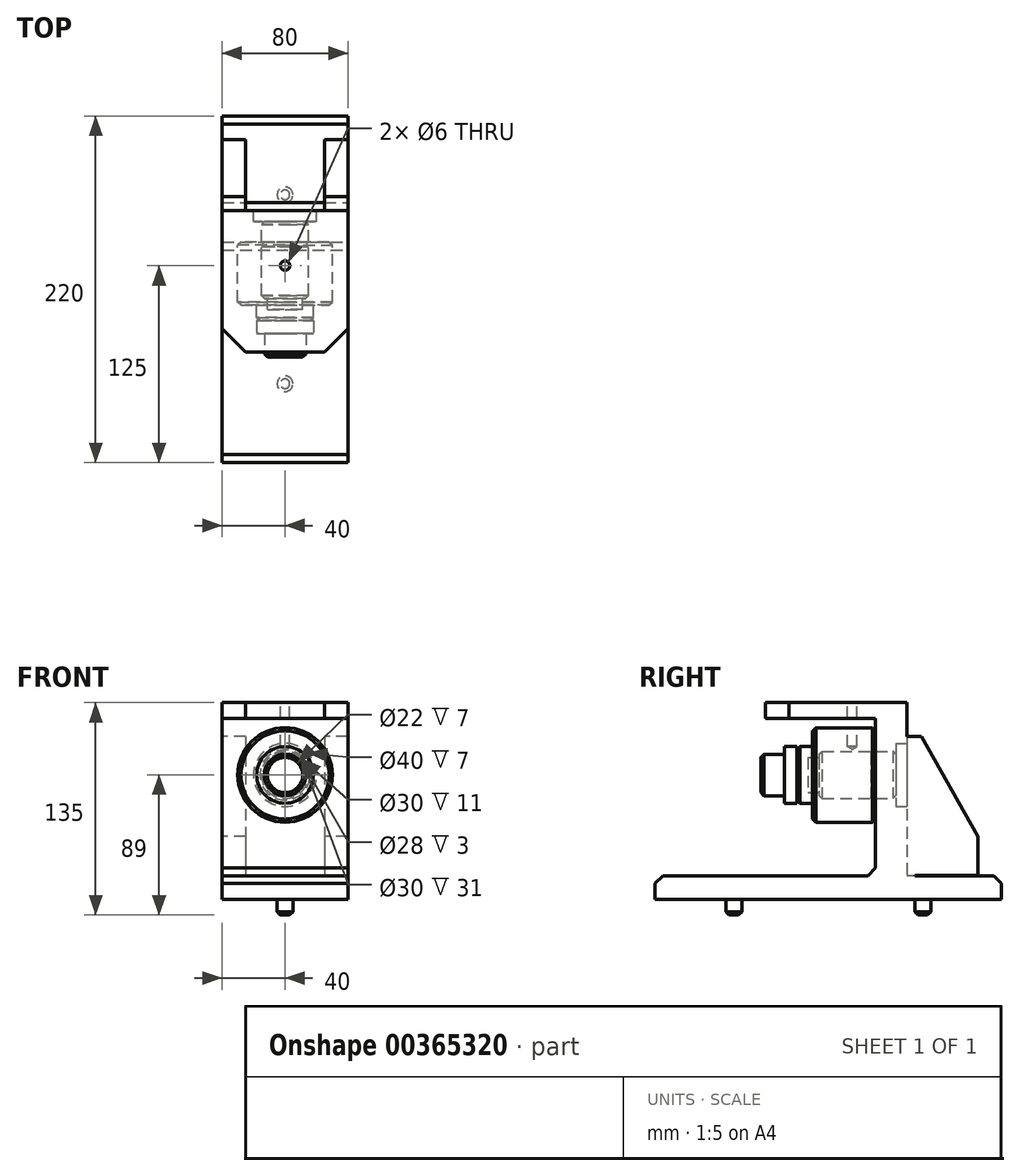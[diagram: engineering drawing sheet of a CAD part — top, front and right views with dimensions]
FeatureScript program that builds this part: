
annotation { "Feature Type Name" : "Feature", "Feature Type Description" : "" }
export const myFeature = defineFeature(function(context is Context, id is Id, definition is map)
    precondition{}
    {
        {
            var Q0;
            Q0=qCreatedBy(makeId("Right.planeOp"),FACE);
            var sketch = newSketch(context, id + "F0", { "sketchPlane" : qUnion([Q0])});
            skLineSegment(sketch, "E0", {"start": v(-10, 11) * mm, "end": v(-10, 18) * mm});
            skLineSegment(sketch, "E1", {"start": v(-10, 18) * mm, "end": v(0, 18) * mm});
            skLineSegment(sketch, "E2", {"start": v(0, 18) * mm, "end": v(0, 30) * mm});
            skLineSegment(sketch, "E3", {"start": v(0, 30) * mm, "end": v(40, 30) * mm});
            skLineSegment(sketch, "E4", {"start": v(40, 30) * mm, "end": v(40, 11) * mm});
            skLineSegment(sketch, "E5", {"start": v(40, 0) * mm, "end": v(-10, 0) * mm});
            skLineSegment(sketch, "E6", {"start": v(-10, 11) * mm, "end": v(40, 11) * mm});
            skSolve(sketch);
        }
        {
            var Q0;
            Q0=makeQuery(id+"F0.imprint","IMPRINT",FACE,{"disambiguationData":[TD([[makeQuery(id+"F0.imprint","IMPRINT",EDGE,{"derivedFrom":sQuery(id+"F0.wireOp",EDGE,"E0")}),-1.0]])]});
            var Q1;
            Q1=sQuery(id+"F0.wireOp",EDGE,"E5");
            revolve(context, id + "F1", {"entities" : qUnion([Q0]), "axis" : qUnion([Q1]), "revolveType" : RevolveType.FULL});
        }
        {
            var Q0;
            Q0=makeQuery(id+"F1.opRevolve","SWEPT_EDGE",EDGE,{"disambiguationData":[OSD([sQuery(id+"F0.wireOp",EDGE,"E0"),sQuery(id+"F0.wireOp",EDGE,"E1")])]});
            var Q1;
            Q1=makeQuery(id+"F1.opRevolve","SWEPT_EDGE",EDGE,{"disambiguationData":[OSD([sQuery(id+"F0.wireOp",EDGE,"E2"),sQuery(id+"F0.wireOp",EDGE,"E3")])]});
            var Q2;
            Q2=makeQuery(id+"F1.opRevolve","SWEPT_EDGE",EDGE,{"disambiguationData":[OSD([sQuery(id+"F0.wireOp",EDGE,"E3"),sQuery(id+"F0.wireOp",EDGE,"E4")])]});
            chamfer(context, id + "F2", {"entities" : qUnion([Q0, Q1, Q2]), "width" : 2 * mm, "tangentPropagation" : true});
        }
        {
            var Q0;
            Q0=qCreatedBy(makeId("Right.planeOp"),FACE);
            var sketch = newSketch(context, id + "F3", { "sketchPlane" : qUnion([Q0])});
            skLineSegment(sketch, "E7", {"start": v(25, 16.27) * mm, "end": v(25, 30) * mm});
            skLineSegment(sketch, "E8", {"start": v(22, 18) * mm, "end": v(22, 30) * mm});
            skLineSegment(sketch, "E9", {"start": v(22, 18) * mm, "end": v(25, 16.27) * mm});
            skPoint(sketch, "E10.orphan", {"position": v(22, 0) * mm});
            skPoint(sketch, "E11.orphan", {"position": v(25, 0) * mm});
            skLineSegment(sketch, "E12", {"start": v(22, 30) * mm, "end": v(25, 30) * mm});
            skSolve(sketch);
        }
        {
            var Q0;
            Q0 = qSketchRegion(id + "F3", true);
            var Q1;
            Q1=sQuery(id+"F3.wireOp",EDGE,"E7");
            revolve(context, id + "F4", {"operationType" : NewBodyOperationType.REMOVE, "entities" : qUnion([Q0]), "axis" : qUnion([Q1]), "revolveType" : RevolveType.FULL, "oppositeDirection" : true});
        }
        {
            var Q0;
            Q0=qCreatedBy(makeId("Top.planeOp"),FACE);
            cPlane(context, id + "F5", {"entities" : qUnion([Q0]), "cplaneType" : CPlaneType.OFFSET, "offset" : 46 * mm, "width" : 150 * mm, "height" : 150 * mm});
        }
        {
            var Q0;
            Q0=qCreatedBy(makeId("Right.planeOp"),FACE);
            var sketch = newSketch(context, id + "F6", { "sketchPlane" : qUnion([Q0])});
            skLineSegment(sketch, "E13", {"start": v(22, 36) * mm, "end": v(22, 46) * mm});
            skLineSegment(sketch, "E14", {"start": v(20, 36) * mm, "end": v(20, 46) * mm});
            skLineSegment(sketch, "E15", {"start": v(20, 46) * mm, "end": v(22, 46) * mm});
            skLineSegment(sketch, "E16", {"start": v(20, 36) * mm, "end": v(22, 36) * mm});
            skPoint(sketch, "E17.orphan", {"position": v(20, 0) * mm});
            skPoint(sketch, "E18.orphan", {"position": v(22, 0) * mm});
            skLineSegment(sketch, "E19", {"start": v(25, 45.98) * mm, "end": v(25, 35.98) * mm});
            skSolve(sketch);
        }
        {
            var Q0;
            Q0 = qSketchRegion(id + "F6", true);
            var Q1;
            Q1=sQuery(id+"F6.wireOp",EDGE,"E19");
            revolve(context, id + "F7", {"entities" : qUnion([Q0]), "axis" : qUnion([Q1]), "revolveType" : RevolveType.FULL});
        }
        {
            var Q0;
            Q0=qCreatedBy(id+"F5.planeOp",FACE);
            var sketch = newSketch(context, id + "F8", { "sketchPlane" : qUnion([Q0])});
            skLineSegment(sketch, "E20.bottom", {"start": v(-40, 60) * mm, "end": v(40, 60) * mm});
            skLineSegment(sketch, "E20.top", {"start": v(-40, -30) * mm, "end": v(40, -30) * mm});
            skLineSegment(sketch, "E20.left", {"start": v(-40, 60) * mm, "end": v(-40, -30) * mm});
            skLineSegment(sketch, "E20.right", {"start": v(40, 60) * mm, "end": v(40, -30) * mm});
            skCircle(sketch, "E21", {"center": v(0, 25) * mm, "radius": 5 * mm});
            skSolve(sketch);
        }
        {
            var Q0;
            Q0=makeQuery(id+"F8.imprint","IMPRINT",FACE,{"disambiguationData":[TD([[makeQuery(id+"F8.imprint","IMPRINT",EDGE,{"derivedFrom":sQuery(id+"F8.wireOp",EDGE,"E20.bottom")}),-1.0]])]});
            extrude(context, id + "F9", {"entities" : qUnion([Q0]), "operationType" : NewBodyOperationType.ADD, "oppositeDirection" : true, "depth" : 10 * mm});
        }
        {
            var Q0;
            Q0=makeQuery(id+"F9.opExtrude","SWEPT_EDGE",EDGE,{"disambiguationData":[OSD([sQuery(id+"F8.wireOp",EDGE,"E20.top"),sQuery(id+"F8.wireOp",EDGE,"E20.left")])]});
            var Q1;
            Q1=makeQuery(id+"F9.opExtrude","SWEPT_EDGE",EDGE,{"disambiguationData":[OSD([sQuery(id+"F8.wireOp",EDGE,"E20.top"),sQuery(id+"F8.wireOp",EDGE,"E20.right")])]});
            chamfer(context, id + "F10", {"entities" : qUnion([Q0, Q1]), "width" : 15 * mm, "tangentPropagation" : true});
        }
        {
            var Q0;
            Q0=qCreatedBy(makeId("Front.planeOp"),FACE);
            cPlane(context, id + "F11", {"entities" : qUnion([Q0]), "cplaneType" : CPlaneType.OFFSET, "offset" : 60 * mm, "oppositeDirection" : true, "width" : 150 * mm, "height" : 150 * mm});
        }
        {
            var Q0;
            Q0=qCreatedBy(id+"F11.planeOp",FACE);
            var sketch = newSketch(context, id + "F12", { "sketchPlane" : qUnion([Q0])});
            skLineSegment(sketch, "E22.bottom", {"start": v(-40, 36) * mm, "end": v(40, 36) * mm});
            skLineSegment(sketch, "E22.top", {"start": v(-40, -64) * mm, "end": v(40, -64) * mm});
            skLineSegment(sketch, "E22.left", {"start": v(-40, 36) * mm, "end": v(-40, -64) * mm});
            skLineSegment(sketch, "E22.right", {"start": v(40, 36) * mm, "end": v(40, -64) * mm});
            skSolve(sketch);
        }
        {
            var Q0;
            Q0=makeQuery(id+"F12.imprint","IMPRINT",FACE,{"disambiguationData":[TD([[makeQuery(id+"F12.imprint","IMPRINT",EDGE,{"derivedFrom":sQuery(id+"F12.wireOp",EDGE,"E22.bottom")}),-1.0]])]});
            extrude(context, id + "F13", {"entities" : qUnion([Q0]), "operationType" : NewBodyOperationType.ADD, "depth" : 20 * mm});
        }
        {
            var Q0;
            Q0=makeQuery(id+"F13.boolean.opBoolean","MERGE",FACE,{"derivedFrom":[makeQuery(id+"F9.opExtrude","SWEPT_FACE",FACE,{"disambiguationData":[OSD([sQuery(id+"F8.wireOp",EDGE,"E20.right")])]}),makeQuery(id+"F13.opExtrude","SWEPT_FACE",FACE,{"disambiguationData":[OSD([sQuery(id+"F12.wireOp",EDGE,"E22.right")])]})]});
            var sketch = newSketch(context, id + "F14", { "sketchPlane" : qUnion([Q0])});
            skLineSegment(sketch, "E23", {"start": v(40, -64) * mm, "end": v(35, -64) * mm});
            skLineSegment(sketch, "E24", {"start": v(35, -64) * mm, "end": v(40, -59) * mm});
            skLineSegment(sketch, "E25", {"start": v(60, -64) * mm, "end": v(65, -64) * mm});
            skLineSegment(sketch, "E26", {"start": v(65, -64) * mm, "end": v(60, -59) * mm});
            skSolve(sketch);
        }
        {
            var Q0;
            {var subQ0=sQuery(id+"F14.wireOp",EDGE,"E23");Q0=makeQuery(id+"F14.imprint","IMPRINT",FACE,{"disambiguationData":[TD([[makeQuery(id+"F14.imprint","IMPRINT",EDGE,{"derivedFrom":subQ0}),-1.0]])]});}
            var Q1;
            {var subQ0=sQuery(id+"F14.wireOp",EDGE,"E25");Q1=makeQuery(id+"F14.imprint","IMPRINT",FACE,{"disambiguationData":[TD([[makeQuery(id+"F14.imprint","IMPRINT",EDGE,{"derivedFrom":subQ0}),1.0]])]});}
            extrude(context, id + "F15", {"entities" : qUnion([Q0, Q1]), "operationType" : NewBodyOperationType.ADD, "oppositeDirection" : true, "depth" : 80 * mm});
        }
        {
            var Q0;
            Q0=qCreatedBy(makeId("Right.planeOp"),FACE);
            var sketch = newSketch(context, id + "F16", { "sketchPlane" : qUnion([Q0])});
            skLineSegment(sketch, "E27", {"start": v(60, 24.53) * mm, "end": v(69, 24.53) * mm});
            skLineSegment(sketch, "E28", {"start": v(69, 24.53) * mm, "end": v(105, -38.95) * mm});
            skLineSegment(sketch, "E29", {"start": v(105, -38.95) * mm, "end": v(105, -63.95) * mm});
            skLineSegment(sketch, "E30", {"start": v(60, -63.95) * mm, "end": v(105, -63.95) * mm});
            skLineSegment(sketch, "E31", {"start": v(60, 24.53) * mm, "end": v(60, -63.95) * mm});
            skSolve(sketch);
        }
        {
            var Q0;
            Q0=qCreatedBy(makeId("Front.planeOp"),FACE);
            var sketch = newSketch(context, id + "F17", { "sketchPlane" : qUnion([Q0])});
            skLineSegment(sketch, "E32.bottom", {"start": v(-40, -64) * mm, "end": v(40, -64) * mm});
            skLineSegment(sketch, "E32.top", {"start": v(-40, -79) * mm, "end": v(40, -79) * mm});
            skLineSegment(sketch, "E32.left", {"start": v(-40, -64) * mm, "end": v(-40, -79) * mm});
            skLineSegment(sketch, "E32.right", {"start": v(40, -64) * mm, "end": v(40, -79) * mm});
            skSolve(sketch);
        }
        {
            var Q0;
            Q0=makeQuery(id+"F17.imprint","IMPRINT",FACE,{"disambiguationData":[TD([[makeQuery(id+"F17.imprint","IMPRINT",EDGE,{"derivedFrom":sQuery(id+"F17.wireOp",EDGE,"E32.bottom")}),-1.0]])]});
            extrude(context, id + "F18", {"entities" : qUnion([Q0]), "operationType" : NewBodyOperationType.ADD, "oppositeDirection" : true, "depth" : 120 * mm, "hasSecondDirection" : true, "secondDirectionOppositeDirection" : false, "secondDirectionDepth" : 100 * mm});
        }
        {
            var Q0;
            Q0=makeQuery(id+"F18.opExtrude","CAP_EDGE",EDGE,{"disambiguationData":[OSD([sQuery(id+"F17.wireOp",EDGE,"E32.bottom")])],"isStart":false});
            var Q1;
            Q1=makeQuery(id+"F18.opExtrude","CAP_EDGE",EDGE,{"disambiguationData":[OSD([sQuery(id+"F17.wireOp",EDGE,"E32.bottom")])],"isStart":true});
            chamfer(context, id + "F19", {"entities" : qUnion([Q0, Q1]), "width" : 5 * mm, "tangentPropagation" : true});
        }
        {
            var Q0;
            Q0=makeQuery(id+"F18.opExtrude","SWEPT_FACE",FACE,{"disambiguationData":[OSD([sQuery(id+"F17.wireOp",EDGE,"E32.top")])]});
            var sketch = newSketch(context, id + "F20", { "sketchPlane" : qUnion([Q0])});
            skCircle(sketch, "E33", {"center": v(0, 50) * mm, "radius": 5 * mm});
            skCircle(sketch, "E34", {"center": v(0, -70) * mm, "radius": 5 * mm});
            skSolve(sketch);
        }
        {
            var Q0;
            Q0=makeQuery(id+"F20.imprint","IMPRINT",FACE,{"disambiguationData":[TD([[makeQuery(id+"F20.imprint","IMPRINT",EDGE,{"derivedFrom":sQuery(id+"F20.wireOp",EDGE,"E33")}),1.0]])]});
            var Q1;
            Q1=makeQuery(id+"F20.imprint","IMPRINT",FACE,{"disambiguationData":[TD([[makeQuery(id+"F20.imprint","IMPRINT",EDGE,{"derivedFrom":sQuery(id+"F20.wireOp",EDGE,"E34")}),1.0]])]});
            extrude(context, id + "F21", {"entities" : qUnion([Q0, Q1]), "operationType" : NewBodyOperationType.ADD, "depth" : 10 * mm});
        }
        {
            var Q0;
            Q0=makeQuery(id+"F21.opExtrude","CAP_EDGE",EDGE,{"disambiguationData":[OSD([sQuery(id+"F20.wireOp",EDGE,"E33")])],"isStart":false});
            var Q1;
            Q1=makeQuery(id+"F21.opExtrude","CAP_EDGE",EDGE,{"disambiguationData":[OSD([sQuery(id+"F20.wireOp",EDGE,"E34")])],"isStart":false});
            chamfer(context, id + "F22", {"entities" : qUnion([Q0, Q1]), "width" : 2 * mm, "tangentPropagation" : true});
        }
        {
            var Q0;
            Q0=makeQuery(id+"F16.imprint","IMPRINT",FACE,{"disambiguationData":[TD([[makeQuery(id+"F16.imprint","IMPRINT",EDGE,{"derivedFrom":sQuery(id+"F16.wireOp",EDGE,"E27")}),-1.0]])]});
            extrude(context, id + "F23", {"entities" : qUnion([Q0]), "operationType" : NewBodyOperationType.ADD, "depth" : 40 * mm, "hasSecondDirection" : true, "secondDirectionOppositeDirection" : true, "secondDirectionDepth" : 40 * mm});
        }
        {
            var Q0;
            Q0 = qSketchRegion(id + "F16", true);
            extrude(context, id + "F24", {"entities" : qUnion([Q0]), "operationType" : NewBodyOperationType.REMOVE, "depth" : 25 * mm, "hasSecondDirection" : true, "secondDirectionOppositeDirection" : true, "secondDirectionDepth" : 25 * mm});
        }
        {
            var Q0;
            Q0=qCreatedBy(makeId("Right.planeOp"),FACE);
            var sketch = newSketch(context, id + "F25", { "sketchPlane" : qUnion([Q0])});
            skLineSegment(sketch, "E35", {"start": v(60, 20) * mm, "end": v(53, 20) * mm});
            skLineSegment(sketch, "E36", {"start": v(53, 20) * mm, "end": v(53, 0) * mm});
            skLineSegment(sketch, "E37", {"start": v(60, 20) * mm, "end": v(60, 0) * mm});
            skLineSegment(sketch, "E38", {"start": v(53, 0) * mm, "end": v(60, 0) * mm});
            skPoint(sketch, "E38.endSnap0", {"position": v(60, 0) * mm});
            skPoint(sketch, "E39.orphan", {"position": v(62.1, 0) * mm});
            skPoint(sketch, "E40.end.orphan", {"position": v(60, -20) * mm});
            skPoint(sketch, "E40.start.orphan", {"position": v(53, -20) * mm});
            skSolve(sketch);
        }
        {
            var Q0;
            Q0 = qSketchRegion(id + "F25", true);
            var Q1;
            Q1=sQuery(id+"F25.wireOp",EDGE,"E38");
            revolve(context, id + "F26", {"operationType" : NewBodyOperationType.REMOVE, "entities" : qUnion([Q0]), "axis" : qUnion([Q1]), "revolveType" : RevolveType.FULL, "oppositeDirection" : true});
        }
        {
            var Q0;
            Q0=qCreatedBy(makeId("Right.planeOp"),FACE);
            var sketch = newSketch(context, id + "F27", { "sketchPlane" : qUnion([Q0])});
            skLineSegment(sketch, "E41", {"start": v(51, 15) * mm, "end": v(40, 15) * mm});
            skLineSegment(sketch, "E42", {"start": v(40, 15) * mm, "end": v(40, 14) * mm});
            skLineSegment(sketch, "E43", {"start": v(40, 14) * mm, "end": v(37, 14) * mm});
            skLineSegment(sketch, "E44", {"start": v(37, 14) * mm, "end": v(37, 15) * mm});
            skLineSegment(sketch, "E45", {"start": v(37, 15) * mm, "end": v(6, 15) * mm});
            skLineSegment(sketch, "E46", {"start": v(4, 13) * mm, "end": v(4, 0) * mm});
            skLineSegment(sketch, "E47", {"start": v(4, 0) * mm, "end": v(53, 0) * mm});
            skLineSegment(sketch, "E48", {"start": v(53, 13) * mm, "end": v(53, 0) * mm});
            skLineSegment(sketch, "E49", {"start": v(51, 15) * mm, "end": v(53, 13) * mm});
            skLineSegment(sketch, "E50", {"start": v(6, 15) * mm, "end": v(4, 13) * mm});
            skPoint(sketch, "E51.orphan", {"position": v(53, 15) * mm});
            skPoint(sketch, "E52.orphan", {"position": v(4, 15) * mm});
            skSolve(sketch);
        }
        {
            var Q0;
            Q0 = qSketchRegion(id + "F27", true);
            var Q1;
            Q1=sQuery(id+"F27.wireOp",EDGE,"E47");
            revolve(context, id + "F28", {"operationType" : NewBodyOperationType.REMOVE, "entities" : qUnion([Q0]), "axis" : qUnion([Q1]), "revolveType" : RevolveType.FULL, "oppositeDirection" : true});
        }
        {
            var Q0;
            Q0=qCreatedBy(makeId("Right.planeOp"),FACE);
            var sketch = newSketch(context, id + "F29", { "sketchPlane" : qUnion([Q0])});
            skLineSegment(sketch, "E53", {"start": v(-18, 13.18) * mm, "end": v(-18, 18) * mm});
            skLineSegment(sketch, "E54", {"start": v(-18, 18) * mm, "end": v(-10, 18) * mm});
            skLineSegment(sketch, "E55", {"start": v(-10, 18) * mm, "end": v(-10, 11) * mm});
            skLineSegment(sketch, "E56", {"start": v(-3, 11) * mm, "end": v(-10, 11) * mm});
            skLineSegment(sketch, "E57", {"start": v(-3, 11) * mm, "end": v(-3, 0) * mm});
            skPoint(sketch, "E58.orphan", {"position": v(-10, 0) * mm});
            skLineSegment(sketch, "E59", {"start": v(-18, 13.18) * mm, "end": v(-33, 13.18) * mm});
            skLineSegment(sketch, "E60", {"start": v(-33, 13.18) * mm, "end": v(-33, 0) * mm});
            skLineSegment(sketch, "E61", {"start": v(-33, 0) * mm, "end": v(-3, 0) * mm});
            skPoint(sketch, "E62.orphan", {"position": v(-18, 0) * mm});
            skSolve(sketch);
        }
        {
            var Q0;
            Q0=makeQuery(id+"F29.imprint","IMPRINT",FACE,{"disambiguationData":[TD([[makeQuery(id+"F29.imprint","IMPRINT",EDGE,{"derivedFrom":sQuery(id+"F29.wireOp",EDGE,"E53")}),-1.0]])]});
            var Q1;
            Q1=sQuery(id+"F29.wireOp",EDGE,"E61");
            revolve(context, id + "F30", {"operationType" : NewBodyOperationType.ADD, "entities" : qUnion([Q0]), "axis" : qUnion([Q1]), "revolveType" : RevolveType.FULL});
        }
        {
            var Q0;
            Q0=makeQuery(id+"F30.opRevolve","SWEPT_EDGE",EDGE,{"disambiguationData":[OSD([sQuery(id+"F29.wireOp",EDGE,"E59"),sQuery(id+"F29.wireOp",EDGE,"E60")])]});
            chamfer(context, id + "F31", {"entities" : qUnion([Q0]), "width" : 2 * mm, "tangentPropagation" : true});
        }
    });
